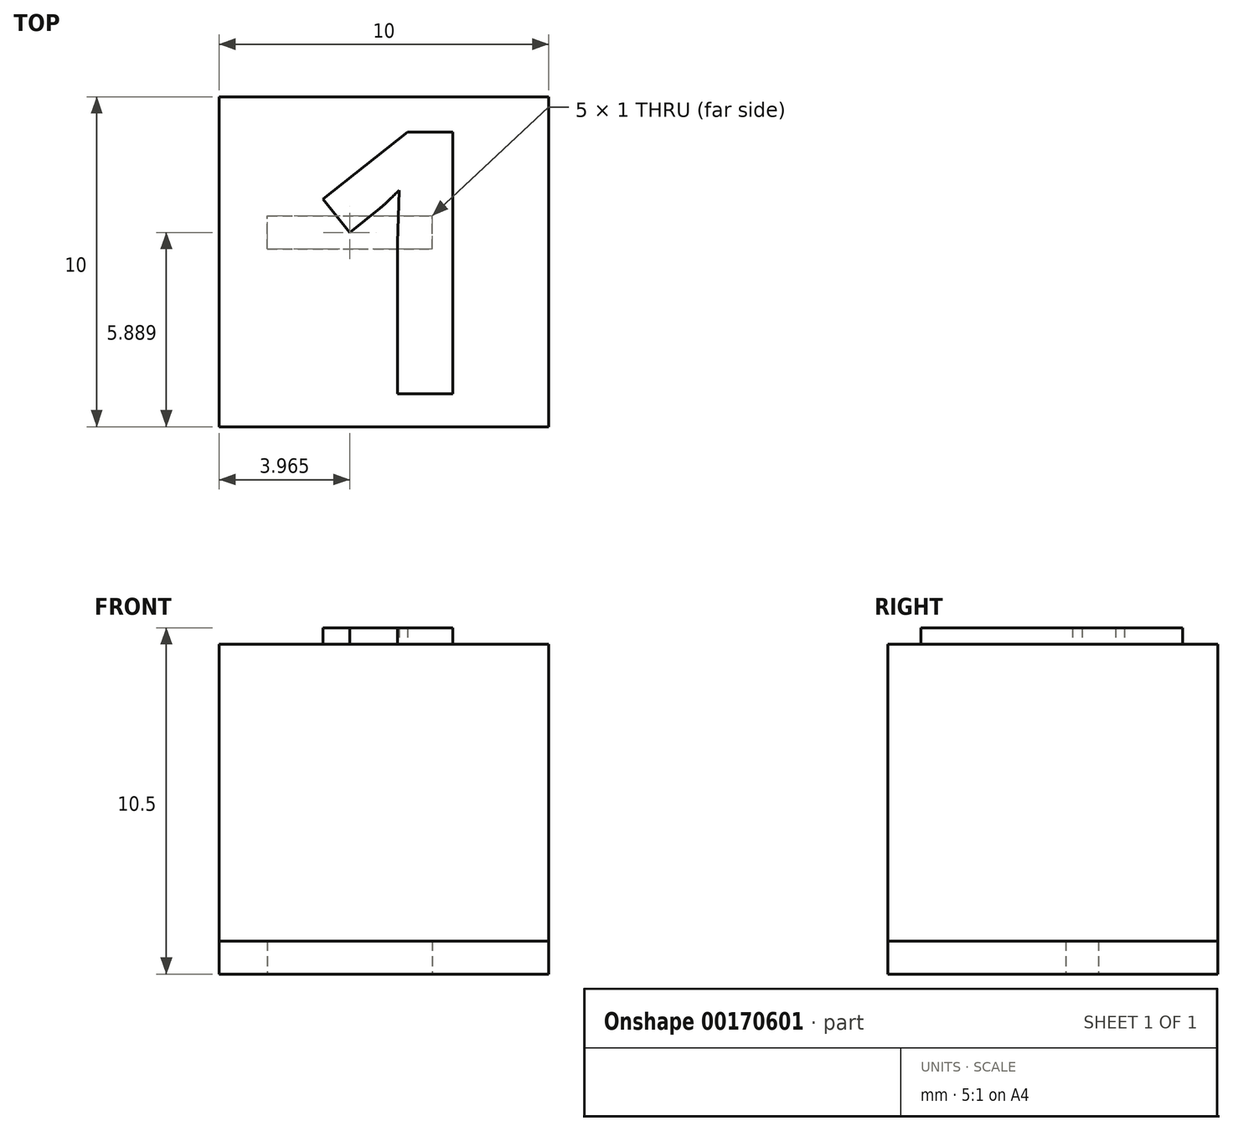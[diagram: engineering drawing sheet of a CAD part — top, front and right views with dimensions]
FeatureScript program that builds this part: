
annotation { "Feature Type Name" : "Feature", "Feature Type Description" : "" }
export const myFeature = defineFeature(function(context is Context, id is Id, definition is map)
    precondition{}
    {
        {
            var Q0;
            Q0=qCreatedBy(makeId("Top.planeOp"),FACE);
            var sketch = newSketch(context, id + "F0", { "sketchPlane" : qUnion([Q0])});
            skLineSegment(sketch, "E0.bottom", {"start": v(0, 0) * mm, "end": v(10, 0) * mm});
            skLineSegment(sketch, "E0.top", {"start": v(0, 10) * mm, "end": v(10, 10) * mm});
            skLineSegment(sketch, "E0.left", {"start": v(0, 0) * mm, "end": v(0, 10) * mm});
            skLineSegment(sketch, "E0.right", {"start": v(10, 0) * mm, "end": v(10, 10) * mm});
            skSolve(sketch);
        }
        {
            var Q0;
            Q0=makeQuery(id+"F0.imprint","IMPRINT",FACE,{"disambiguationData":[TD([[makeQuery(id+"F0.imprint","IMPRINT",EDGE,{"derivedFrom":sQuery(id+"F0.wireOp",EDGE,"E0.bottom")}),1.0]])]});
            extrude(context, id + "F1", {"entities" : qUnion([Q0]), "depth" : 10 * mm});
        }
        {
            var Q0;
            Q0=makeQuery(id+"F1.opExtrude","CAP_FACE",FACE,{"disambiguationData":[OSD([sQuery(id+"F0.wireOp",EDGE,"E0.bottom"),sQuery(id+"F0.wireOp",EDGE,"E0.top"),sQuery(id+"F0.wireOp",EDGE,"E0.left"),sQuery(id+"F0.wireOp",EDGE,"E0.right")])],"isStart":false});
            var sketch = newSketch(context, id + "F2", { "sketchPlane" : qUnion([Q0])});
            skText(sketch, "E1", { "text": "1", "fontName": "OpenSans-Bold.ttf"});
            const initialGuessF2  = {"E1": [0.0025, 0.001, 1, 0, 0.008]};
            skSetInitialGuess(sketch, initialGuessF2);
            skSolve(sketch);
        }
        {
            var Q0;
            Q0=qSketchRegion(id+"F2",true);
            extrude(context, id + "F3", {"entities" : qUnion([Q0]), "operationType" : NewBodyOperationType.ADD, "depth" : 0.5 * mm});
        }
        {
            var Q0;
            Q0=makeQuery(id+"F1.opExtrude","CAP_FACE",FACE,{"disambiguationData":[OSD([sQuery(id+"F0.wireOp",EDGE,"E0.bottom"),sQuery(id+"F0.wireOp",EDGE,"E0.top"),sQuery(id+"F0.wireOp",EDGE,"E0.left"),sQuery(id+"F0.wireOp",EDGE,"E0.right")])],"isStart":true});
            var sketch = newSketch(context, id + "F4", { "sketchPlane" : qUnion([Q0])});
            skLineSegment(sketch, "E2.bottom", {"start": v(1.47, -5.39) * mm, "end": v(6.47, -5.39) * mm});
            skLineSegment(sketch, "E2.top", {"start": v(1.47, -6.39) * mm, "end": v(6.47, -6.39) * mm});
            skLineSegment(sketch, "E2.left", {"start": v(1.47, -5.39) * mm, "end": v(1.47, -6.39) * mm});
            skLineSegment(sketch, "E2.right", {"start": v(6.47, -5.39) * mm, "end": v(6.47, -6.39) * mm});
            skPoint(sketch, "E2.middle", {"position": v(3.97, -5.89) * mm});
            skSolve(sketch);
        }
        {
            var Q0;
            Q0 = qSketchRegion(id + "F4", true);
            extrude(context, id + "F5", {"entities" : qUnion([Q0]), "operationType" : NewBodyOperationType.REMOVE, "oppositeDirection" : true, "depth" : 1 * mm});
        }
        {
            var Q0;
            Q0=makeQuery(id+"F1.opExtrude","CAP_FACE",FACE,{"disambiguationData":[OSD([sQuery(id+"F0.wireOp",EDGE,"E0.bottom"),sQuery(id+"F0.wireOp",EDGE,"E0.top"),sQuery(id+"F0.wireOp",EDGE,"E0.left"),sQuery(id+"F0.wireOp",EDGE,"E0.right")])],"isStart":true});
            var sketch = newSketch(context, id + "F6", { "sketchPlane" : qUnion([Q0])});
            skLineSegment(sketch, "E3.0.0", {"start": v(0, 0) * mm, "end": v(0, -10) * mm});
            skLineSegment(sketch, "E3.0.1", {"start": v(0, -10) * mm, "end": v(10, -10) * mm});
            skLineSegment(sketch, "E3.0.2", {"start": v(10, -10) * mm, "end": v(10, 0) * mm});
            skLineSegment(sketch, "E3.0.3", {"start": v(10, 0) * mm, "end": v(0, 0) * mm});
            skLineSegment(sketch, "E4.bottom", {"start": v(6.47, -6.39) * mm, "end": v(1.47, -6.39) * mm});
            skLineSegment(sketch, "E4.top", {"start": v(6.47, -5.39) * mm, "end": v(1.47, -5.39) * mm});
            skLineSegment(sketch, "E4.left", {"start": v(6.47, -6.39) * mm, "end": v(6.47, -5.39) * mm});
            skLineSegment(sketch, "E4.right", {"start": v(1.47, -6.39) * mm, "end": v(1.47, -5.39) * mm});
            skSolve(sketch);
        }
        {
            var Q0;
            Q0 = qSketchRegion(id + "F6", true);
            extrude(context, id + "F7", {"entities" : qUnion([Q0]), "oppositeDirection" : true, "depth" : 1 * mm});
        }
    });
